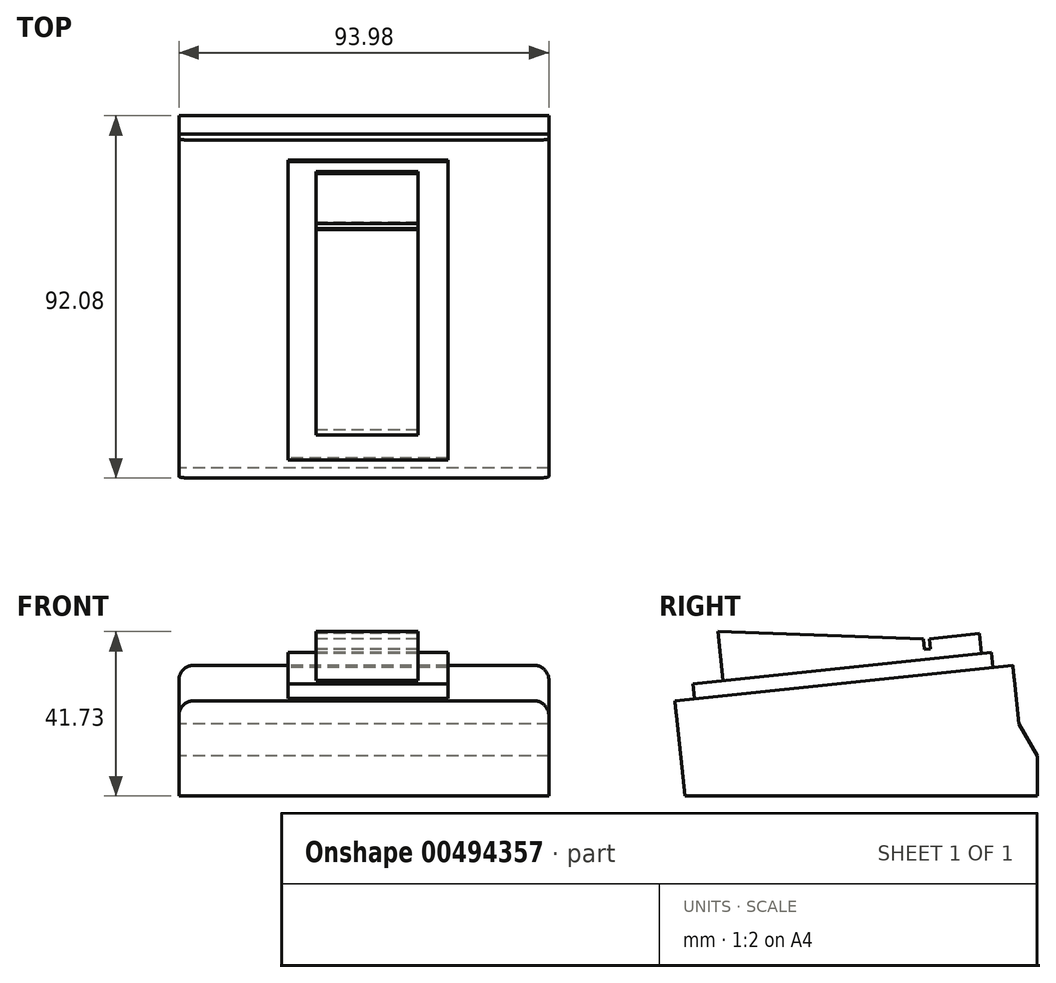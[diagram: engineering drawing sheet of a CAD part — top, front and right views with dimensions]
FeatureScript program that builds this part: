
annotation { "Feature Type Name" : "Feature", "Feature Type Description" : "" }
export const myFeature = defineFeature(function(context is Context, id is Id, definition is map)
    precondition{}
    {
        {
            var Q0;
            Q0=qCreatedBy(makeId("Right.planeOp"),FACE);
            var sketch = newSketch(context, id + "F0", { "sketchPlane" : qUnion([Q0])});
            skLineSegment(sketch, "E0", {"start": v(2.54, 0) * mm, "end": v(92.08, 0) * mm});
            skLineSegment(sketch, "E1", {"start": v(92.08, 0) * mm, "end": v(92.08, 10.16) * mm});
            skLineSegment(sketch, "E2", {"start": v(92.08, 10.16) * mm, "end": v(87.43, 18.21) * mm});
            skLineSegment(sketch, "E3", {"start": v(87.43, 18.21) * mm, "end": v(85.85, 33.19) * mm});
            skLineSegment(sketch, "E4", {"start": v(85.85, 33.19) * mm, "end": v(0, 24.17) * mm});
            skLineSegment(sketch, "E5", {"start": v(0, 24.17) * mm, "end": v(2.54, 0) * mm});
            skLineSegment(sketch, "E6", {"start": v(80.8, 32.66) * mm, "end": v(80.4, 36.45) * mm});
            skLineSegment(sketch, "E7", {"start": v(80.4, 36.45) * mm, "end": v(4.65, 28.49) * mm});
            skLineSegment(sketch, "E8", {"start": v(4.65, 28.49) * mm, "end": v(5.05, 24.7) * mm});
            skLineSegment(sketch, "E9", {"start": v(77.87, 36.18) * mm, "end": v(77.34, 41.23) * mm});
            skLineSegment(sketch, "E10", {"start": v(77.34, 41.23) * mm, "end": v(64.71, 39.9) * mm});
            skLineSegment(sketch, "E11", {"start": v(64.71, 39.9) * mm, "end": v(64.98, 37.38) * mm});
            skLineSegment(sketch, "E12", {"start": v(64.98, 37.38) * mm, "end": v(63.46, 37.22) * mm});
            skLineSegment(sketch, "E13", {"start": v(63.46, 37.22) * mm, "end": v(63.18, 39.9) * mm});
            skLineSegment(sketch, "E14", {"start": v(63.18, 39.9) * mm, "end": v(10.92, 41.73) * mm});
            skLineSegment(sketch, "E15", {"start": v(10.92, 41.73) * mm, "end": v(12.23, 29.28) * mm});
            skSolve(sketch);
        }
        {
            var Q0;
            Q0=makeQuery(id+"F0.imprint","IMPRINT",FACE,{"disambiguationData":[TD([[makeQuery(id+"F0.imprint","IMPRINT",EDGE,{"derivedFrom":sQuery(id+"F0.wireOp",EDGE,"E0")}),1.0]])]});
            extrude(context, id + "F1", {"entities" : qUnion([Q0]), "depth" : 93.98 * mm});
        }
        {
            var Q0;
            {var subQ1=sQuery(id+"F0.wireOp",EDGE,"E6");Q0=makeQuery(id+"F0.imprint","IMPRINT",FACE,{"disambiguationData":[TD([[makeQuery(id+"F0.imprint","IMPRINT",EDGE,{"derivedFrom":subQ1}),1.0]])]});}
            extrude(context, id + "F2", {"entities" : qUnion([Q0]), "depth" : 40.64 * mm});
        }
        {
            var Q0;
            {var subQ0=sQuery(id+"F0.wireOp",EDGE,"E9");Q0=makeQuery(id+"F0.imprint","IMPRINT",FACE,{"disambiguationData":[TD([[makeQuery(id+"F0.imprint","IMPRINT",EDGE,{"derivedFrom":subQ0}),1.0]])]});}
            extrude(context, id + "F3", {"entities" : qUnion([Q0]), "depth" : 25.9 * mm});
        }
        {
            var Q0;
            Q0=makeQuery(id+"F3.opExtrude","SWEPT_BODY",BODY,{"disambiguationData":[OSD([sQuery(id+"F0.wireOp",EDGE,"E7"),sQuery(id+"F0.wireOp",EDGE,"E9"),sQuery(id+"F0.wireOp",EDGE,"E10"),sQuery(id+"F0.wireOp",EDGE,"E11"),sQuery(id+"F0.wireOp",EDGE,"E12"),sQuery(id+"F0.wireOp",EDGE,"E13"),sQuery(id+"F0.wireOp",EDGE,"E14"),sQuery(id+"F0.wireOp",EDGE,"E15")])]});
            transform(context, id + "F4", {"entities" : qUnion([Q0]), "transformType" : TransformType.TRANSLATION_3D, "dx" : 7.11 * mm, "dy" : 0 * mm, "dz" : 0 * mm, "makeCopy" : false});
        }
        {
            var Q0;
            Q0=makeQuery(id+"F2.opExtrude","SWEPT_BODY",BODY,{"disambiguationData":[OSD([sQuery(id+"F0.wireOp",EDGE,"E4"),sQuery(id+"F0.wireOp",EDGE,"E6"),sQuery(id+"F0.wireOp",EDGE,"E7"),sQuery(id+"F0.wireOp",EDGE,"E8")])]});
            var Q1;
            Q1=makeQuery(id+"F3.opExtrude","SWEPT_BODY",BODY,{"disambiguationData":[OSD([sQuery(id+"F0.wireOp",EDGE,"E7"),sQuery(id+"F0.wireOp",EDGE,"E9"),sQuery(id+"F0.wireOp",EDGE,"E10"),sQuery(id+"F0.wireOp",EDGE,"E11"),sQuery(id+"F0.wireOp",EDGE,"E12"),sQuery(id+"F0.wireOp",EDGE,"E13"),sQuery(id+"F0.wireOp",EDGE,"E14"),sQuery(id+"F0.wireOp",EDGE,"E15")])]});
            transform(context, id + "F5", {"entities" : qUnion([Q0, Q1]), "transformType" : TransformType.TRANSLATION_3D, "dx" : 27.7 * mm, "dy" : 0 * mm, "dz" : 0 * mm, "makeCopy" : false});
        }
        {
            var Q0;
            Q0=makeQuery(id+"F1.opExtrude","CAP_EDGE",EDGE,{"disambiguationData":[OSD([sQuery(id+"F0.wireOp",EDGE,"E4")])],"isStart":true});
            var Q1;
            Q1=makeQuery(id+"F1.opExtrude","CAP_EDGE",EDGE,{"disambiguationData":[OSD([sQuery(id+"F0.wireOp",EDGE,"E4")])],"isStart":false});
            fillet(context, id + "F6", {"entities" : qUnion([Q0, Q1]), "radius" : 3.8 * mm, "tangentPropagation" : true, "allowEdgeOverflow" : false});
        }
    });
